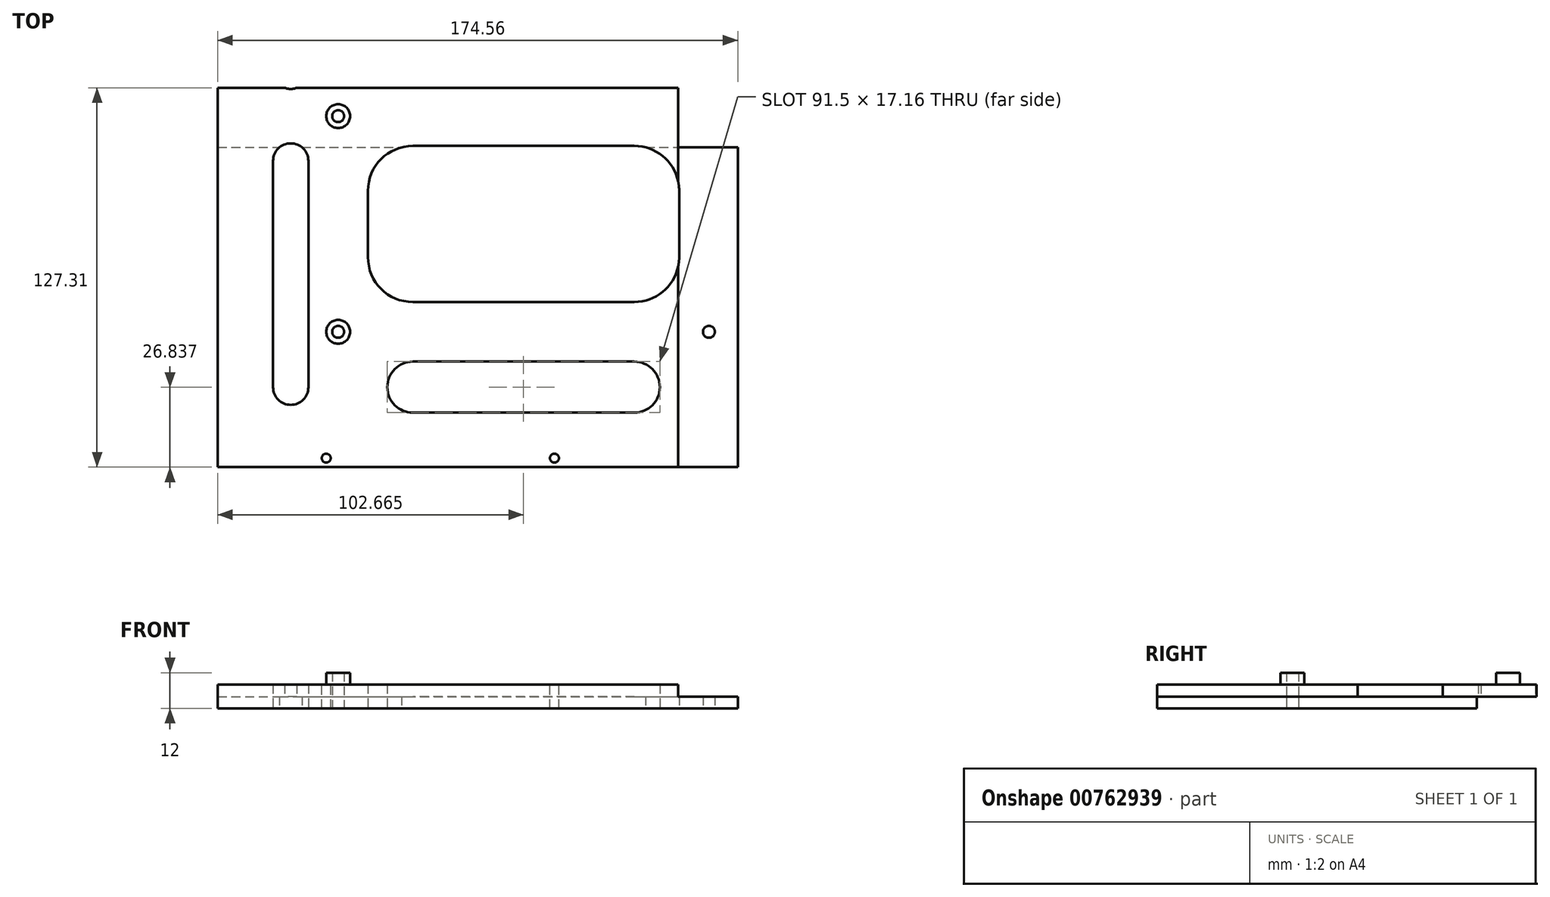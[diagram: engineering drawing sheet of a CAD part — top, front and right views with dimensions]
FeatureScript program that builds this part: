
annotation { "Feature Type Name" : "Feature", "Feature Type Description" : "" }
export const myFeature = defineFeature(function(context is Context, id is Id, definition is map)
    precondition{}
    {
        {
            var Q0;
            Q0=qCreatedBy(makeId("Top.planeOp"),FACE);
            var sketch = newSketch(context, id + "F0", { "sketchPlane" : qUnion([Q0])});
            skLineSegment(sketch, "E0.bottom", {"start": v(-84.85, 211.43) * mm, "end": v(248.95, 211.43) * mm});
            skLineSegment(sketch, "E0.left", {"start": v(-84.85, 211.43) * mm, "end": v(-84.85, -69.57) * mm});
            skLineSegment(sketch, "E0.right", {"start": v(248.95, 211.43) * mm, "end": v(248.95, -32.4) * mm});
            skCircle(sketch, "E1", {"center": v(-44.42, 203.18) * mm, "radius": 2 * mm});
            skCircle(sketch, "E2", {"center": v(-44.42, 48.24) * mm, "radius": 2 * mm});
            skCircle(sketch, "E3", {"center": v(-44.42, -24.15) * mm, "radius": 2 * mm});
            skCircle(sketch, "E4", {"center": v(80.04, -24.15) * mm, "radius": 2 * mm});
            skCircle(sketch, "E5", {"center": v(80.04, 48.24) * mm, "radius": 2 * mm});
            skCircle(sketch, "E6", {"center": v(80.04, 203.18) * mm, "radius": 2 * mm});
            skCircle(sketch, "E7", {"center": v(237.52, 48.24) * mm, "radius": 2 * mm});
            skCircle(sketch, "E8", {"center": v(237.52, -24.15) * mm, "radius": 2 * mm});
            skCircle(sketch, "E9", {"center": v(237.52, 180.32) * mm, "radius": 2 * mm});
            skLineSegment(sketch, "E10.left", {"start": v(-34.42, 178.12) * mm, "end": v(-34.42, 73.3) * mm});
            skLineSegment(sketch, "E10.right", {"start": v(70.04, 178.12) * mm, "end": v(70.04, 73.3) * mm});
            skLineSegment(sketch, "E11.bottom", {"start": v(-19.36, 58.24) * mm, "end": v(54.99, 58.24) * mm});
            skLineSegment(sketch, "E11.top", {"start": v(-19.36, 38.24) * mm, "end": v(54.99, 38.24) * mm});
            skLineSegment(sketch, "E12.left", {"start": v(-34.42, 23.18) * mm, "end": v(-34.42, 0.9) * mm});
            skLineSegment(sketch, "E12.right", {"start": v(70.04, 23.18) * mm, "end": v(70.04, 0.9) * mm});
            skLineSegment(sketch, "E13.left", {"start": v(90.04, 23.18) * mm, "end": v(90.04, 0.9) * mm});
            skLineSegment(sketch, "E13.right", {"start": v(227.52, 23.18) * mm, "end": v(227.52, 0.9) * mm});
            skLineSegment(sketch, "E14.bottom", {"start": v(212.47, -14.15) * mm, "end": v(105.1, -14.15) * mm});
            skLineSegment(sketch, "E14.top", {"start": v(212.47, 38.24) * mm, "end": v(105.1, 38.24) * mm});
            skLineSegment(sketch, "E15.bottom", {"start": v(212.47, 58.24) * mm, "end": v(105.1, 58.24) * mm});
            skLineSegment(sketch, "E15.top", {"start": v(212.47, 193.18) * mm, "end": v(105.1, 193.18) * mm});
            skLineSegment(sketch, "E16.left", {"start": v(90.04, 178.12) * mm, "end": v(90.04, 73.3) * mm});
            skLineSegment(sketch, "E17", {"start": v(-19.36, -14.15) * mm, "end": v(54.99, -14.15) * mm});
            skLineSegment(sketch, "E18", {"start": v(-19.36, 193.18) * mm, "end": v(54.99, 193.18) * mm});
            skLineSegment(sketch, "E19", {"start": v(212.47, 170.32) * mm, "end": v(212.47, 193.18) * mm});
            skLineSegment(sketch, "E20", {"start": v(227.52, 155.26) * mm, "end": v(227.52, 73.3) * mm});
            skLineSegment(sketch, "E21", {"start": v(54.99, -34.15) * mm, "end": v(-19.36, -34.15) * mm});
            skLineSegment(sketch, "E22.MirrorCS", {"start": v(212.47, -51.31) * mm, "end": v(105.1, -51.31) * mm});
            skLineSegment(sketch, "E23.MirrorCS", {"start": v(212.47, -34.15) * mm, "end": v(105.1, -34.15) * mm});
            skLineSegment(sketch, "E24.MirrorCS", {"start": v(-19.36, -51.31) * mm, "end": v(54.99, -51.31) * mm});
            skLineSegment(sketch, "E25", {"start": v(-84.85, -69.57) * mm, "end": v(248.95, -69.57) * mm});
            skLineSegment(sketch, "E26", {"start": v(248.95, -32.4) * mm, "end": v(248.95, -69.57) * mm});
            skLineSegment(sketch, "E27", {"start": v(-54.42, -42.73) * mm, "end": v(-54.42, 33.18) * mm});
            skLineSegment(sketch, "E28", {"start": v(-66.28, 33.18) * mm, "end": v(-66.28, -42.73) * mm});
            skArc(sketch, "E29", {"start": v(-54.42, 33.18) * mm, "mid": v(-60.35, 39.1) * mm, "end": v(-66.28, 33.18) * mm});
            skArc(sketch, "E30", {"start": v(-66.28, -42.73) * mm, "mid": v(-60.35, -48.66) * mm, "end": v(-54.42, -42.73) * mm});
            skArc(sketch, "E31", {"start": v(-34.42, 0.9) * mm, "mid": v(-30, -9.74) * mm, "end": v(-19.36, -14.15) * mm});
            skArc(sketch, "E32", {"start": v(-19.36, 38.24) * mm, "mid": v(-30, 33.83) * mm, "end": v(-34.42, 23.18) * mm});
            skArc(sketch, "E33", {"start": v(70.04, 23.18) * mm, "mid": v(65.63, 33.83) * mm, "end": v(54.99, 38.24) * mm});
            skArc(sketch, "E34", {"start": v(54.99, -14.15) * mm, "mid": v(65.63, -9.74) * mm, "end": v(70.04, 0.9) * mm});
            skArc(sketch, "E35", {"start": v(-19.36, -34.15) * mm, "mid": v(-27.94, -42.73) * mm, "end": v(-19.36, -51.31) * mm});
            skArc(sketch, "E36", {"start": v(54.99, -51.31) * mm, "mid": v(63.56, -42.73) * mm, "end": v(54.99, -34.15) * mm});
            skArc(sketch, "E37", {"start": v(105.1, -34.15) * mm, "mid": v(96.52, -42.73) * mm, "end": v(105.1, -51.31) * mm});
            skArc(sketch, "E38", {"start": v(212.47, -51.31) * mm, "mid": v(221.04, -42.73) * mm, "end": v(212.47, -34.15) * mm});
            skArc(sketch, "E39", {"start": v(212.47, -14.15) * mm, "mid": v(223.11, -9.74) * mm, "end": v(227.52, 0.9) * mm});
            skArc(sketch, "E40", {"start": v(227.52, 23.18) * mm, "mid": v(223.11, 33.83) * mm, "end": v(212.47, 38.24) * mm});
            skArc(sketch, "E41", {"start": v(105.1, 38.24) * mm, "mid": v(94.46, 33.83) * mm, "end": v(90.04, 23.18) * mm});
            skArc(sketch, "E42", {"start": v(90.04, 0.9) * mm, "mid": v(94.46, -9.74) * mm, "end": v(105.1, -14.15) * mm});
            skArc(sketch, "E43", {"start": v(105.1, 193.18) * mm, "mid": v(94.46, 188.77) * mm, "end": v(90.04, 178.12) * mm});
            skArc(sketch, "E44", {"start": v(70.04, 178.12) * mm, "mid": v(65.63, 188.77) * mm, "end": v(54.99, 193.18) * mm});
            skArc(sketch, "E45", {"start": v(-19.36, 193.18) * mm, "mid": v(-30, 188.77) * mm, "end": v(-34.42, 178.12) * mm});
            skArc(sketch, "E46", {"start": v(-34.42, 73.3) * mm, "mid": v(-30, 62.65) * mm, "end": v(-19.36, 58.24) * mm});
            skArc(sketch, "E47", {"start": v(54.99, 58.24) * mm, "mid": v(65.63, 62.65) * mm, "end": v(70.04, 73.3) * mm});
            skArc(sketch, "E48", {"start": v(90.04, 73.3) * mm, "mid": v(94.46, 62.65) * mm, "end": v(105.1, 58.24) * mm});
            skArc(sketch, "E49", {"start": v(212.47, 58.24) * mm, "mid": v(223.11, 62.65) * mm, "end": v(227.52, 73.3) * mm});
            skArc(sketch, "E50", {"start": v(227.52, 155.26) * mm, "mid": v(223.11, 165.9) * mm, "end": v(212.47, 170.32) * mm});
            skArc(sketch, "E51.MirrorCS", {"start": v(-54.42, 63.3) * mm, "mid": v(-60.35, 57.36) * mm, "end": v(-66.28, 63.3) * mm});
            skLineSegment(sketch, "E52.MirrorCS", {"start": v(-66.28, 63.3) * mm, "end": v(-66.28, 180.32) * mm});
            skLineSegment(sketch, "E53.MirrorCS", {"start": v(-54.42, 180.32) * mm, "end": v(-54.42, 63.3) * mm});
            skArc(sketch, "E54.MirrorCS", {"start": v(-66.28, 180.32) * mm, "mid": v(-60.35, 186.25) * mm, "end": v(-54.42, 180.32) * mm});
            skSolve(sketch);
        }
        {
            var Q0;
            Q0=makeQuery(id+"F0.imprint","IMPRINT",FACE,{"disambiguationData":[TD([[makeQuery(id+"F0.imprint","IMPRINT",EDGE,{"derivedFrom":sQuery(id+"F0.wireOp",EDGE,"E0.bottom")}),-1.0]])]});
            extrude(context, id + "F1", {"entities" : qUnion([Q0]), "depth" : 8 * mm, "offsetDistance" : 25 * mm});
        }
        {
            var Q0;
            Q0=makeQuery(id+"F1.opExtrude","CAP_FACE",FACE,{"disambiguationData":[OSD([sQuery(id+"F0.wireOp",EDGE,"E0.bottom"),sQuery(id+"F0.wireOp",EDGE,"E0.left"),sQuery(id+"F0.wireOp",EDGE,"E0.right"),sQuery(id+"F0.wireOp",EDGE,"E1"),sQuery(id+"F0.wireOp",EDGE,"E2"),sQuery(id+"F0.wireOp",EDGE,"E3"),sQuery(id+"F0.wireOp",EDGE,"E4"),sQuery(id+"F0.wireOp",EDGE,"E5"),sQuery(id+"F0.wireOp",EDGE,"E6"),sQuery(id+"F0.wireOp",EDGE,"E7"),sQuery(id+"F0.wireOp",EDGE,"E8"),sQuery(id+"F0.wireOp",EDGE,"E9"),sQuery(id+"F0.wireOp",EDGE,"E10.left"),sQuery(id+"F0.wireOp",EDGE,"E10.right"),sQuery(id+"F0.wireOp",EDGE,"E11.bottom"),sQuery(id+"F0.wireOp",EDGE,"E11.top"),sQuery(id+"F0.wireOp",EDGE,"E12.left"),sQuery(id+"F0.wireOp",EDGE,"E12.right"),sQuery(id+"F0.wireOp",EDGE,"E13.left"),sQuery(id+"F0.wireOp",EDGE,"E13.right"),sQuery(id+"F0.wireOp",EDGE,"E14.bottom"),sQuery(id+"F0.wireOp",EDGE,"E14.top"),sQuery(id+"F0.wireOp",EDGE,"E15.bottom"),sQuery(id+"F0.wireOp",EDGE,"E15.top"),sQuery(id+"F0.wireOp",EDGE,"E16.left"),sQuery(id+"F0.wireOp",EDGE,"E17"),sQuery(id+"F0.wireOp",EDGE,"E18"),sQuery(id+"F0.wireOp",EDGE,"E19"),sQuery(id+"F0.wireOp",EDGE,"E20"),sQuery(id+"F0.wireOp",EDGE,"E21"),sQuery(id+"F0.wireOp",EDGE,"E22.MirrorCS"),sQuery(id+"F0.wireOp",EDGE,"E23.MirrorCS"),sQuery(id+"F0.wireOp",EDGE,"E24.MirrorCS"),sQuery(id+"F0.wireOp",EDGE,"E25"),sQuery(id+"F0.wireOp",EDGE,"E26"),sQuery(id+"F0.wireOp",EDGE,"E27"),sQuery(id+"F0.wireOp",EDGE,"E28"),sQuery(id+"F0.wireOp",EDGE,"E29"),sQuery(id+"F0.wireOp",EDGE,"E30"),sQuery(id+"F0.wireOp",EDGE,"E31"),sQuery(id+"F0.wireOp",EDGE,"E32"),sQuery(id+"F0.wireOp",EDGE,"E33"),sQuery(id+"F0.wireOp",EDGE,"E34"),sQuery(id+"F0.wireOp",EDGE,"E35"),sQuery(id+"F0.wireOp",EDGE,"E36"),sQuery(id+"F0.wireOp",EDGE,"E37"),sQuery(id+"F0.wireOp",EDGE,"E38"),sQuery(id+"F0.wireOp",EDGE,"E39"),sQuery(id+"F0.wireOp",EDGE,"E40"),sQuery(id+"F0.wireOp",EDGE,"E41"),sQuery(id+"F0.wireOp",EDGE,"E42"),sQuery(id+"F0.wireOp",EDGE,"E43"),sQuery(id+"F0.wireOp",EDGE,"E44"),sQuery(id+"F0.wireOp",EDGE,"E45"),sQuery(id+"F0.wireOp",EDGE,"E46"),sQuery(id+"F0.wireOp",EDGE,"E47"),sQuery(id+"F0.wireOp",EDGE,"E48"),sQuery(id+"F0.wireOp",EDGE,"E49"),sQuery(id+"F0.wireOp",EDGE,"E50"),sQuery(id+"F0.wireOp",EDGE,"E51.MirrorCS"),sQuery(id+"F0.wireOp",EDGE,"E52.MirrorCS"),sQuery(id+"F0.wireOp",EDGE,"E53.MirrorCS"),sQuery(id+"F0.wireOp",EDGE,"E54.MirrorCS")])],"isStart":false});
            var sketch = newSketch(context, id + "F2", { "sketchPlane" : qUnion([Q0])});
            skLineSegment(sketch, "E55.bottom", {"start": v(-84.85, 211.43) * mm, "end": v(15.15, 211.43) * mm});
            skLineSegment(sketch, "E55.top", {"start": v(-84.85, 71.43) * mm, "end": v(-81.85, 71.43) * mm});
            skLineSegment(sketch, "E55.left", {"start": v(-84.85, 211.43) * mm, "end": v(-84.85, 71.43) * mm});
            skLineSegment(sketch, "E55.right", {"start": v(15.15, 211.43) * mm, "end": v(15.15, 208.43) * mm});
            skLineSegment(sketch, "E56", {"start": v(-81.85, 208.43) * mm, "end": v(-81.85, 71.43) * mm});
            skLineSegment(sketch, "E57", {"start": v(-81.85, 208.43) * mm, "end": v(15.15, 208.43) * mm});
            skSolve(sketch);
        }
        {
            var Q0;
            Q0=makeQuery(id+"F2.imprint","IMPRINT",FACE,{"disambiguationData":[TD([[makeQuery(id+"F2.imprint","IMPRINT",EDGE,{"derivedFrom":sQuery(id+"F2.wireOp",EDGE,"E55.bottom")}),-1.0]])]});
            extrude(context, id + "F3", {"entities" : qUnion([Q0]), "operationType" : NewBodyOperationType.ADD, "depth" : 185 * mm, "offsetDistance" : 25 * mm});
        }
        {
            var Q0;
            Q0=makeQuery(id+"F3.boolean.opBoolean","MERGE",FACE,{"derivedFrom":[makeQuery(id+"F1.opExtrude","SWEPT_FACE",FACE,{"disambiguationData":[OSD([sQuery(id+"F0.wireOp",EDGE,"E0.left")])]}),makeQuery(id+"F3.opExtrude","SWEPT_FACE",FACE,{"disambiguationData":[OSD([sQuery(id+"F2.wireOp",EDGE,"E55.left")])]})]});
            var sketch = newSketch(context, id + "F4", { "sketchPlane" : qUnion([Q0])});
            skLineSegment(sketch, "E58", {"start": v(-211.43, 193) * mm, "end": v(-206.43, 193) * mm});
            skLineSegment(sketch, "E59", {"start": v(-206.43, 193) * mm, "end": v(-158.54, 40) * mm});
            skLineSegment(sketch, "E60.1", {"start": v(-201.43, 143.55) * mm, "end": v(-169.02, 40) * mm});
            skLineSegment(sketch, "E61.trimOffspring", {"start": v(-201.43, 143.55) * mm, "end": v(-201.43, 40) * mm});
            skLineSegment(sketch, "E62", {"start": v(-211.43, 0) * mm, "end": v(-211.43, 58.72) * mm});
            skLineSegment(sketch, "E63", {"start": v(-60.87, 0) * mm, "end": v(-60.87, 40) * mm});
            skLineSegment(sketch, "E64", {"start": v(-60.87, 40) * mm, "end": v(-158.54, 40) * mm});
            skPoint(sketch, "E65.orphan", {"position": v(-211.43, 40) * mm});
            skLineSegment(sketch, "E66.trimOffspring", {"start": v(-169.02, 40) * mm, "end": v(-201.43, 40) * mm});
            skLineSegment(sketch, "E67", {"start": v(-60.87, 0) * mm, "end": v(-211.43, 0) * mm});
            skSolve(sketch);
        }
        {
            var Q0;
            Q0=makeQuery(id+"F4.imprint","IMPRINT",FACE,{"disambiguationData":[TD([[makeQuery(id+"F4.imprint","IMPRINT",EDGE,{"derivedFrom":sQuery(id+"F4.wireOp",EDGE,"E60.1")}),-1.0]])]});
            var Q1;
            {var subQ0=sQuery(id+"F4.wireOp",EDGE,"E59");Q1=makeQuery(id+"F4.imprint","IMPRINT",FACE,{"disambiguationData":[TD([[makeQuery(id+"F4.imprint","IMPRINT",EDGE,{"derivedFrom":subQ0}),1.0]])]});}
            extrude(context, id + "F5", {"entities" : qUnion([Q0, Q1]), "operationType" : NewBodyOperationType.REMOVE, "oppositeDirection" : true, "depth" : 5 * mm, "offsetDistance" : 25 * mm});
        }
        {
            var Q0;
            Q0=makeQuery(id+"F1.opExtrude","CAP_FACE",FACE,{"disambiguationData":[OSD([sQuery(id+"F0.wireOp",EDGE,"E0.bottom"),sQuery(id+"F0.wireOp",EDGE,"E0.left"),sQuery(id+"F0.wireOp",EDGE,"E0.right"),sQuery(id+"F0.wireOp",EDGE,"E1"),sQuery(id+"F0.wireOp",EDGE,"E2"),sQuery(id+"F0.wireOp",EDGE,"E3"),sQuery(id+"F0.wireOp",EDGE,"E4"),sQuery(id+"F0.wireOp",EDGE,"E5"),sQuery(id+"F0.wireOp",EDGE,"E6"),sQuery(id+"F0.wireOp",EDGE,"E7"),sQuery(id+"F0.wireOp",EDGE,"E8"),sQuery(id+"F0.wireOp",EDGE,"E9"),sQuery(id+"F0.wireOp",EDGE,"E10.left"),sQuery(id+"F0.wireOp",EDGE,"E10.right"),sQuery(id+"F0.wireOp",EDGE,"E11.bottom"),sQuery(id+"F0.wireOp",EDGE,"E11.top"),sQuery(id+"F0.wireOp",EDGE,"E12.left"),sQuery(id+"F0.wireOp",EDGE,"E12.right"),sQuery(id+"F0.wireOp",EDGE,"E13.left"),sQuery(id+"F0.wireOp",EDGE,"E13.right"),sQuery(id+"F0.wireOp",EDGE,"E14.bottom"),sQuery(id+"F0.wireOp",EDGE,"E14.top"),sQuery(id+"F0.wireOp",EDGE,"E15.bottom"),sQuery(id+"F0.wireOp",EDGE,"E15.top"),sQuery(id+"F0.wireOp",EDGE,"E16.left"),sQuery(id+"F0.wireOp",EDGE,"E17"),sQuery(id+"F0.wireOp",EDGE,"E18"),sQuery(id+"F0.wireOp",EDGE,"E19"),sQuery(id+"F0.wireOp",EDGE,"E20"),sQuery(id+"F0.wireOp",EDGE,"E21"),sQuery(id+"F0.wireOp",EDGE,"E22.MirrorCS"),sQuery(id+"F0.wireOp",EDGE,"E23.MirrorCS"),sQuery(id+"F0.wireOp",EDGE,"E24.MirrorCS"),sQuery(id+"F0.wireOp",EDGE,"E25"),sQuery(id+"F0.wireOp",EDGE,"E26"),sQuery(id+"F0.wireOp",EDGE,"E27"),sQuery(id+"F0.wireOp",EDGE,"E28"),sQuery(id+"F0.wireOp",EDGE,"E29"),sQuery(id+"F0.wireOp",EDGE,"E30"),sQuery(id+"F0.wireOp",EDGE,"E31"),sQuery(id+"F0.wireOp",EDGE,"E32"),sQuery(id+"F0.wireOp",EDGE,"E33"),sQuery(id+"F0.wireOp",EDGE,"E34"),sQuery(id+"F0.wireOp",EDGE,"E35"),sQuery(id+"F0.wireOp",EDGE,"E36"),sQuery(id+"F0.wireOp",EDGE,"E37"),sQuery(id+"F0.wireOp",EDGE,"E38"),sQuery(id+"F0.wireOp",EDGE,"E39"),sQuery(id+"F0.wireOp",EDGE,"E40"),sQuery(id+"F0.wireOp",EDGE,"E41"),sQuery(id+"F0.wireOp",EDGE,"E42"),sQuery(id+"F0.wireOp",EDGE,"E43"),sQuery(id+"F0.wireOp",EDGE,"E44"),sQuery(id+"F0.wireOp",EDGE,"E45"),sQuery(id+"F0.wireOp",EDGE,"E46"),sQuery(id+"F0.wireOp",EDGE,"E47"),sQuery(id+"F0.wireOp",EDGE,"E48"),sQuery(id+"F0.wireOp",EDGE,"E49"),sQuery(id+"F0.wireOp",EDGE,"E50"),sQuery(id+"F0.wireOp",EDGE,"E51.MirrorCS"),sQuery(id+"F0.wireOp",EDGE,"E52.MirrorCS"),sQuery(id+"F0.wireOp",EDGE,"E53.MirrorCS"),sQuery(id+"F0.wireOp",EDGE,"E54.MirrorCS")])],"isStart":false});
            var sketch = newSketch(context, id + "F6", { "sketchPlane" : qUnion([Q0])});
            skCircle(sketch, "E68", {"center": v(80.04, 203.18) * mm, "radius": 2 * mm});
            skCircle(sketch, "E69.0", {"center": v(80.04, 203.18) * mm, "radius": 4 * mm});
            skLineSegment(sketch, "E70.0", {"start": v(243.95, -64.57) * mm, "end": v(243.95, 206.43) * mm});
            skLineSegment(sketch, "E70.1", {"start": v(-79.85, -64.57) * mm, "end": v(243.95, -64.57) * mm});
            skLineSegment(sketch, "E70.2", {"start": v(243.95, 206.43) * mm, "end": v(20.15, 206.43) * mm});
            skLineSegment(sketch, "E70.3", {"start": v(-79.85, 66.43) * mm, "end": v(-79.85, -64.57) * mm});
            skLineSegment(sketch, "E70.4", {"start": v(20.15, 206.43) * mm, "end": v(20.15, 203.43) * mm});
            skLineSegment(sketch, "E70.5", {"start": v(20.15, 203.43) * mm, "end": v(-76.85, 203.43) * mm});
            skLineSegment(sketch, "E70.6", {"start": v(-76.85, 203.43) * mm, "end": v(-76.85, 66.43) * mm});
            skLineSegment(sketch, "E70.7", {"start": v(-76.85, 66.43) * mm, "end": v(-79.85, 66.43) * mm});
            skCircle(sketch, "E71.0", {"center": v(237.52, 180.32) * mm, "radius": 4 * mm});
            skCircle(sketch, "E72.0", {"center": v(237.52, 48.24) * mm, "radius": 4 * mm});
            skCircle(sketch, "E73.0", {"center": v(80.04, 48.24) * mm, "radius": 4 * mm});
            skCircle(sketch, "E74.0", {"center": v(237.52, -24.15) * mm, "radius": 4 * mm});
            skCircle(sketch, "E75.0", {"center": v(80.04, -24.15) * mm, "radius": 4 * mm});
            skCircle(sketch, "E76.0", {"center": v(-44.42, -24.15) * mm, "radius": 4 * mm});
            skCircle(sketch, "E77.0", {"center": v(-44.42, 48.24) * mm, "radius": 4 * mm});
            skCircle(sketch, "E78.0", {"center": v(-44.42, 203.18) * mm, "radius": 4 * mm});
            skSolve(sketch);
        }
        {
            var Q0;
            Q0=makeQuery(id+"F6.imprint","IMPRINT",FACE,{"disambiguationData":[TD([[makeQuery(id+"F6.imprint","IMPRINT",EDGE,{"derivedFrom":sQuery(id+"F6.wireOp",EDGE,"E77.0")}),1.0]])]});
            var Q1;
            Q1=makeQuery(id+"F6.imprint","IMPRINT",FACE,{"disambiguationData":[TD([[makeQuery(id+"F6.imprint","IMPRINT",EDGE,{"derivedFrom":sQuery(id+"F6.wireOp",EDGE,"E76.0")}),1.0]])]});
            extrude(context, id + "F7", {"entities" : qUnion([Q0, Q1]), "operationType" : NewBodyOperationType.ADD, "depth" : 4 * mm, "offsetDistance" : 25 * mm});
        }
        {
            var Q0;
            Q0=makeQuery(id+"F1.opExtrude","SWEPT_FACE",FACE,{"disambiguationData":[OSD([sQuery(id+"F0.wireOp",EDGE,"E0.right"),sQuery(id+"F0.wireOp",EDGE,"E26")])]});
            var sketch = newSketch(context, id + "F8", { "sketchPlane" : qUnion([Q0])});
            skLineSegment(sketch, "E79.left", {"start": v(37.74, 4) * mm, "end": v(37.74, 0) * mm});
            skLineSegment(sketch, "E79.right", {"start": v(57.74, 8) * mm, "end": v(57.74, 4) * mm});
            skLineSegment(sketch, "E80", {"start": v(37.74, 4) * mm, "end": v(57.74, 4) * mm});
            skLineSegment(sketch, "E81.top", {"start": v(57.74, 198.6) * mm, "end": v(218.52, 198.6) * mm});
            skLineSegment(sketch, "E81.left", {"start": v(57.74, 8) * mm, "end": v(57.74, 198.6) * mm});
            skLineSegment(sketch, "E81.right", {"start": v(218.52, 0) * mm, "end": v(218.52, 198.6) * mm});
            skLineSegment(sketch, "E82", {"start": v(37.74, 0) * mm, "end": v(218.52, 0) * mm});
            skSolve(sketch);
        }
        {
            var Q0;
            {var subQ3=sQuery(id+"F8.wireOp",EDGE,"E79.left");Q0=makeQuery(id+"F8.imprint","IMPRINT",FACE,{"disambiguationData":[TD([[makeQuery(id+"F8.imprint","IMPRINT",EDGE,{"derivedFrom":subQ3}),1.0]])]});}
            extrude(context, id + "F9", {"entities" : qUnion([Q0]), "operationType" : NewBodyOperationType.REMOVE, "oppositeDirection" : true, "depth" : 340 * mm, "offsetDistance" : 25 * mm});
        }
        {
            var Q0;
            Q0=makeQuery(id+"F3.boolean.opBoolean","MERGE",FACE,{"derivedFrom":[makeQuery(id+"F1.opExtrude","SWEPT_FACE",FACE,{"disambiguationData":[OSD([sQuery(id+"F0.wireOp",EDGE,"E0.bottom")])]}),makeQuery(id+"F3.opExtrude","SWEPT_FACE",FACE,{"disambiguationData":[OSD([sQuery(id+"F2.wireOp",EDGE,"E55.bottom")])]})]});
            var sketch = newSketch(context, id + "F10", { "sketchPlane" : qUnion([Q0])});
            skLineSegment(sketch, "E83.left", {"start": v(-69.71, 4) * mm, "end": v(-69.71, 8) * mm});
            skLineSegment(sketch, "E83.right", {"start": v(-89.71, 0) * mm, "end": v(-89.71, 4) * mm});
            skLineSegment(sketch, "E84", {"start": v(-89.71, 4) * mm, "end": v(-69.71, 4) * mm});
            skLineSegment(sketch, "E85", {"start": v(-69.71, 8) * mm, "end": v(-270.75, 8) * mm});
            skLineSegment(sketch, "E86", {"start": v(-270.75, 8) * mm, "end": v(-270.75, -15.38) * mm});
            skLineSegment(sketch, "E87", {"start": v(-270.75, -15.38) * mm, "end": v(-89.71, 0) * mm});
            skSolve(sketch);
        }
        {
            var Q0;
            Q0=qSketchRegion(id+"F10",true);
            var Q1;
            {var subQ3=sQuery(id+"F10.wireOp",EDGE,"E83.left");Q1=makeQuery(id+"F10.imprint","IMPRINT",FACE,{"disambiguationData":[TD([[makeQuery(id+"F10.imprint","IMPRINT",EDGE,{"derivedFrom":subQ3}),1.0]])]});}
            extrude(context, id + "F11", {"entities" : qUnion([Q0, Q1]), "operationType" : NewBodyOperationType.REMOVE, "oppositeDirection" : true, "depth" : 320 * mm, "offsetDistance" : 25 * mm});
        }
        {
            var Q0;
            Q0=makeQuery(id+"F9.boolean.opBoolean","COPY",FACE,{"derivedFrom":makeQuery(id+"F9.opExtrude","SWEPT_FACE",FACE,{"disambiguationData":[OSD([sQuery(id+"F0.wireOp",EDGE,"E0.right"),sQuery(id+"F0.wireOp",EDGE,"E26")])]})});
            extrude(context, id + "F12", {"entities" : qUnion([Q0]), "operationType" : NewBodyOperationType.REMOVE, "oppositeDirection" : true, "depth" : 190 * mm, "offsetDistance" : 25 * mm});
        }
        {
            var Q0;
            Q0=makeQuery(id+"F1.opExtrude","CAP_FACE",FACE,{"disambiguationData":[OSD([sQuery(id+"F0.wireOp",EDGE,"E0.bottom"),sQuery(id+"F0.wireOp",EDGE,"E0.left"),sQuery(id+"F0.wireOp",EDGE,"E0.right"),sQuery(id+"F0.wireOp",EDGE,"E1"),sQuery(id+"F0.wireOp",EDGE,"E2"),sQuery(id+"F0.wireOp",EDGE,"E3"),sQuery(id+"F0.wireOp",EDGE,"E4"),sQuery(id+"F0.wireOp",EDGE,"E5"),sQuery(id+"F0.wireOp",EDGE,"E6"),sQuery(id+"F0.wireOp",EDGE,"E7"),sQuery(id+"F0.wireOp",EDGE,"E8"),sQuery(id+"F0.wireOp",EDGE,"E9"),sQuery(id+"F0.wireOp",EDGE,"E10.left"),sQuery(id+"F0.wireOp",EDGE,"E10.right"),sQuery(id+"F0.wireOp",EDGE,"E11.bottom"),sQuery(id+"F0.wireOp",EDGE,"E11.top"),sQuery(id+"F0.wireOp",EDGE,"E12.left"),sQuery(id+"F0.wireOp",EDGE,"E12.right"),sQuery(id+"F0.wireOp",EDGE,"E13.left"),sQuery(id+"F0.wireOp",EDGE,"E13.right"),sQuery(id+"F0.wireOp",EDGE,"E14.bottom"),sQuery(id+"F0.wireOp",EDGE,"E14.top"),sQuery(id+"F0.wireOp",EDGE,"E15.bottom"),sQuery(id+"F0.wireOp",EDGE,"E15.top"),sQuery(id+"F0.wireOp",EDGE,"E16.left"),sQuery(id+"F0.wireOp",EDGE,"E17"),sQuery(id+"F0.wireOp",EDGE,"E18"),sQuery(id+"F0.wireOp",EDGE,"E19"),sQuery(id+"F0.wireOp",EDGE,"E20"),sQuery(id+"F0.wireOp",EDGE,"E21"),sQuery(id+"F0.wireOp",EDGE,"E22.MirrorCS"),sQuery(id+"F0.wireOp",EDGE,"E23.MirrorCS"),sQuery(id+"F0.wireOp",EDGE,"E24.MirrorCS"),sQuery(id+"F0.wireOp",EDGE,"E25"),sQuery(id+"F0.wireOp",EDGE,"E26"),sQuery(id+"F0.wireOp",EDGE,"E27"),sQuery(id+"F0.wireOp",EDGE,"E28"),sQuery(id+"F0.wireOp",EDGE,"E29"),sQuery(id+"F0.wireOp",EDGE,"E30"),sQuery(id+"F0.wireOp",EDGE,"E31"),sQuery(id+"F0.wireOp",EDGE,"E32"),sQuery(id+"F0.wireOp",EDGE,"E33"),sQuery(id+"F0.wireOp",EDGE,"E34"),sQuery(id+"F0.wireOp",EDGE,"E35"),sQuery(id+"F0.wireOp",EDGE,"E36"),sQuery(id+"F0.wireOp",EDGE,"E37"),sQuery(id+"F0.wireOp",EDGE,"E38"),sQuery(id+"F0.wireOp",EDGE,"E39"),sQuery(id+"F0.wireOp",EDGE,"E40"),sQuery(id+"F0.wireOp",EDGE,"E41"),sQuery(id+"F0.wireOp",EDGE,"E42"),sQuery(id+"F0.wireOp",EDGE,"E43"),sQuery(id+"F0.wireOp",EDGE,"E44"),sQuery(id+"F0.wireOp",EDGE,"E45"),sQuery(id+"F0.wireOp",EDGE,"E46"),sQuery(id+"F0.wireOp",EDGE,"E47"),sQuery(id+"F0.wireOp",EDGE,"E48"),sQuery(id+"F0.wireOp",EDGE,"E49"),sQuery(id+"F0.wireOp",EDGE,"E50"),sQuery(id+"F0.wireOp",EDGE,"E51.MirrorCS"),sQuery(id+"F0.wireOp",EDGE,"E52.MirrorCS"),sQuery(id+"F0.wireOp",EDGE,"E53.MirrorCS"),sQuery(id+"F0.wireOp",EDGE,"E54.MirrorCS")])],"isStart":false});
            var sketch = newSketch(context, id + "F13", { "sketchPlane" : qUnion([Q0])});
            skCircle(sketch, "E88", {"center": v(28.17, -66.57) * mm, "radius": 1.5 * mm});
            skCircle(sketch, "E89", {"center": v(-48.43, -66.57) * mm, "radius": 1.5 * mm});
            skSolve(sketch);
        }
        {
            var Q0;
            Q0=makeQuery(id+"F13.imprint","IMPRINT",FACE,{"disambiguationData":[TD([[makeQuery(id+"F13.imprint","IMPRINT",EDGE,{"derivedFrom":sQuery(id+"F13.wireOp",EDGE,"E88")}),1.0]])]});
            var Q1;
            Q1=makeQuery(id+"F13.imprint","IMPRINT",FACE,{"disambiguationData":[TD([[makeQuery(id+"F13.imprint","IMPRINT",EDGE,{"derivedFrom":sQuery(id+"F13.wireOp",EDGE,"E89")}),1.0]])]});
            extrude(context, id + "F14", {"entities" : qUnion([Q0, Q1]), "operationType" : NewBodyOperationType.REMOVE, "oppositeDirection" : true, "depth" : 25 * mm, "offsetDistance" : 25 * mm});
        }
    });
